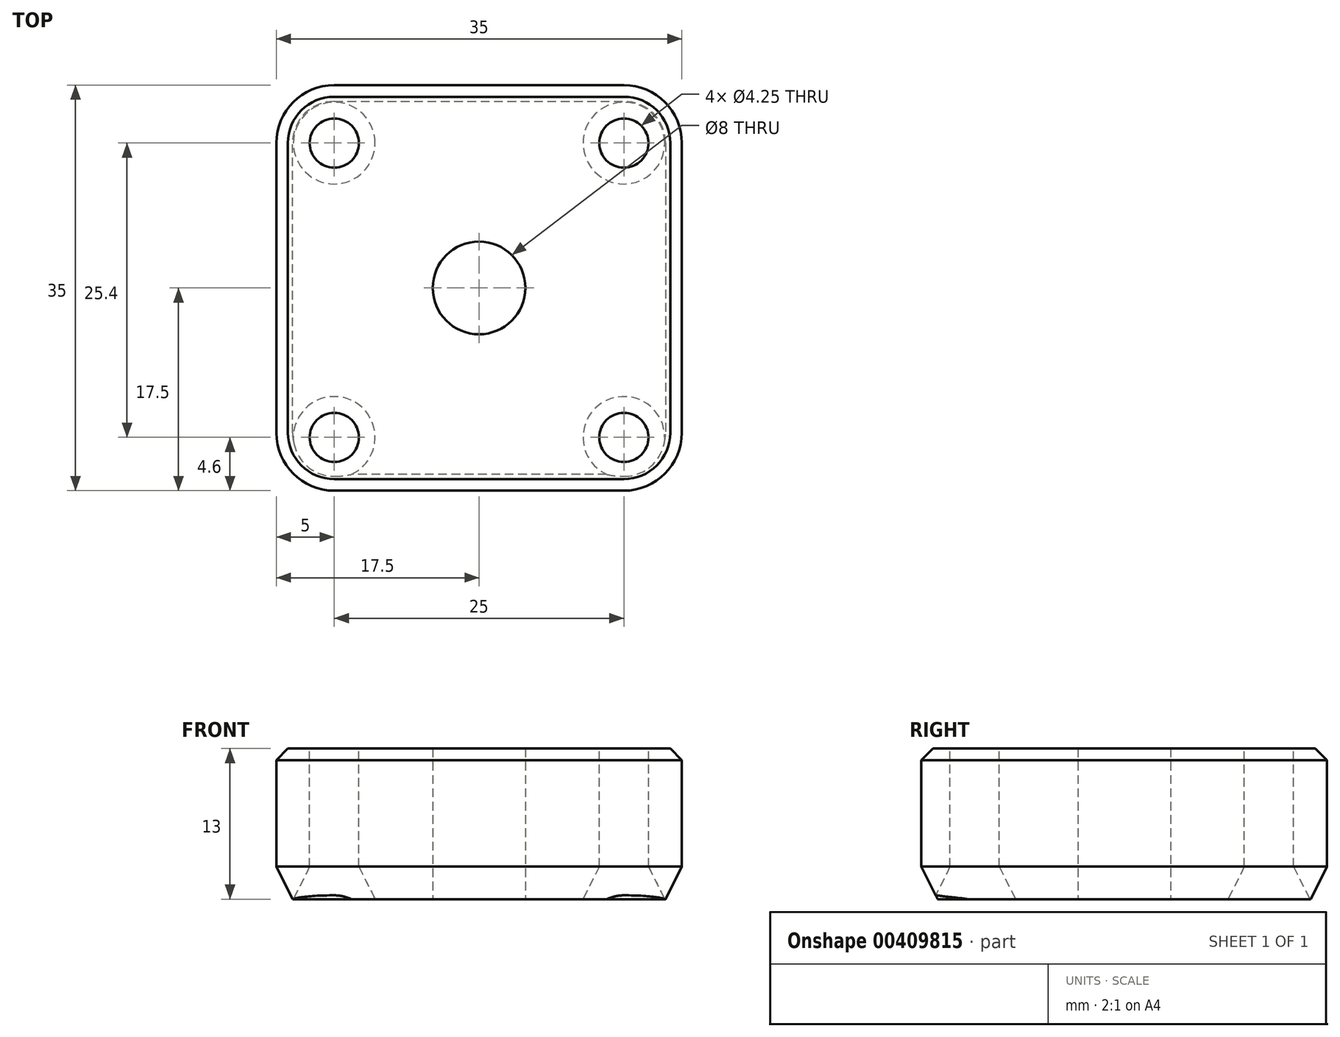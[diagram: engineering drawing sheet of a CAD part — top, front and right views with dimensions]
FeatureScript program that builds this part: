
annotation { "Feature Type Name" : "Feature", "Feature Type Description" : "" }
export const myFeature = defineFeature(function(context is Context, id is Id, definition is map)
    precondition{}
    {
        {
            var Q0;
            Q0=qCreatedBy(makeId("Top.planeOp"),FACE);
            var sketch = newSketch(context, id + "F0", { "sketchPlane" : qUnion([Q0])});
            skLineSegment(sketch, "E0.bottom", {"start": v(17.5, 17.5) * mm, "end": v(-17.5, 17.5) * mm});
            skLineSegment(sketch, "E0.top", {"start": v(17.5, -17.5) * mm, "end": v(-17.5, -17.5) * mm});
            skLineSegment(sketch, "E0.left", {"start": v(17.5, 17.5) * mm, "end": v(17.5, -17.5) * mm});
            skLineSegment(sketch, "E0.right", {"start": v(-17.5, 17.5) * mm, "end": v(-17.5, -17.5) * mm});
            skPoint(sketch, "E0.middle", {"position": v(0, 0) * mm});
            skSolve(sketch);
        }
        {
            var Q0;
            Q0=makeQuery(id+"F0.imprint","IMPRINT",FACE,{"disambiguationData":[TD([[makeQuery(id+"F0.imprint","IMPRINT",EDGE,{"derivedFrom":sQuery(id+"F0.wireOp",EDGE,"E0.bottom")}),1.0]])]});
            extrude(context, id + "F1", {"entities" : qUnion([Q0]), "endBound" : BoundingType.SYMMETRIC, "depth" : 13 * mm});
        }
        {
            var Q0;
            Q0=makeQuery(id+"F1.opExtrude","CAP_FACE",FACE,{"disambiguationData":[OSD([sQuery(id+"F0.wireOp",EDGE,"E0.bottom"),sQuery(id+"F0.wireOp",EDGE,"E0.top"),sQuery(id+"F0.wireOp",EDGE,"E0.left"),sQuery(id+"F0.wireOp",EDGE,"E0.right")])],"isStart":false});
            var sketch = newSketch(context, id + "F2", { "sketchPlane" : qUnion([Q0])});
            skCircle(sketch, "E1", {"center": v(-12.5, -12.9) * mm, "radius": 2.12 * mm});
            skCircle(sketch, "E2", {"center": v(-12.5, 12.5) * mm, "radius": 2.12 * mm});
            skCircle(sketch, "E3", {"center": v(12.5, 12.5) * mm, "radius": 2.12 * mm});
            skCircle(sketch, "E4", {"center": v(12.5, -12.9) * mm, "radius": 2.12 * mm});
            skSolve(sketch);
        }
        {
            var Q0;
            Q0=qSketchRegion(id+"F2",true);
            extrude(context, id + "F3", {"entities" : qUnion([Q0]), "operationType" : NewBodyOperationType.REMOVE, "endBound" : BoundingType.THROUGH_ALL, "oppositeDirection" : true, "depth" : 25 * mm});
        }
        {
            var Q0;
            Q0=makeQuery(id+"F1.opExtrude","SWEPT_EDGE",EDGE,{"disambiguationData":[OSD([sQuery(id+"F0.wireOp",EDGE,"E0.bottom"),sQuery(id+"F0.wireOp",EDGE,"E0.right")])]});
            var Q1;
            Q1=makeQuery(id+"F1.opExtrude","SWEPT_EDGE",EDGE,{"disambiguationData":[OSD([sQuery(id+"F0.wireOp",EDGE,"E0.bottom"),sQuery(id+"F0.wireOp",EDGE,"E0.left")])]});
            var Q2;
            Q2=makeQuery(id+"F1.opExtrude","SWEPT_EDGE",EDGE,{"disambiguationData":[OSD([sQuery(id+"F0.wireOp",EDGE,"E0.top"),sQuery(id+"F0.wireOp",EDGE,"E0.left")])]});
            var Q3;
            Q3=makeQuery(id+"F1.opExtrude","SWEPT_EDGE",EDGE,{"disambiguationData":[OSD([sQuery(id+"F0.wireOp",EDGE,"E0.top"),sQuery(id+"F0.wireOp",EDGE,"E0.right")])]});
            fillet(context, id + "F4", {"entities" : qUnion([Q0, Q1, Q2, Q3]), "radius" : 5 * mm, "tangentPropagation" : true, "allowEdgeOverflow" : false});
        }
        {
            var Q0;
            Q0=makeQuery(id+"F3.boolean.opBoolean","INTERSECT",EDGE,{"derivedFrom":[makeQuery(id+"F1.opExtrude","CAP_FACE",FACE,{"disambiguationData":[OSD([sQuery(id+"F0.wireOp",EDGE,"E0.bottom"),sQuery(id+"F0.wireOp",EDGE,"E0.top"),sQuery(id+"F0.wireOp",EDGE,"E0.left"),sQuery(id+"F0.wireOp",EDGE,"E0.right")])],"isStart":true}),makeQuery(id+"F3.opExtrude","SWEPT_FACE",FACE,{"disambiguationData":[OSD([sQuery(id+"F2.wireOp",EDGE,"E1")])]})]});
            var Q1;
            Q1=makeQuery(id+"F3.boolean.opBoolean","INTERSECT",EDGE,{"derivedFrom":[makeQuery(id+"F1.opExtrude","CAP_FACE",FACE,{"disambiguationData":[OSD([sQuery(id+"F0.wireOp",EDGE,"E0.bottom"),sQuery(id+"F0.wireOp",EDGE,"E0.top"),sQuery(id+"F0.wireOp",EDGE,"E0.left"),sQuery(id+"F0.wireOp",EDGE,"E0.right")])],"isStart":true}),makeQuery(id+"F3.opExtrude","SWEPT_FACE",FACE,{"disambiguationData":[OSD([sQuery(id+"F2.wireOp",EDGE,"E4")])]})]});
            var Q2;
            Q2=makeQuery(id+"F3.boolean.opBoolean","INTERSECT",EDGE,{"derivedFrom":[makeQuery(id+"F1.opExtrude","CAP_FACE",FACE,{"disambiguationData":[OSD([sQuery(id+"F0.wireOp",EDGE,"E0.bottom"),sQuery(id+"F0.wireOp",EDGE,"E0.top"),sQuery(id+"F0.wireOp",EDGE,"E0.left"),sQuery(id+"F0.wireOp",EDGE,"E0.right")])],"isStart":true}),makeQuery(id+"F3.opExtrude","SWEPT_FACE",FACE,{"disambiguationData":[OSD([sQuery(id+"F2.wireOp",EDGE,"E3")])]})]});
            var Q3;
            Q3=makeQuery(id+"F1.opExtrude","CAP_FACE",FACE,{"disambiguationData":[OSD([sQuery(id+"F0.wireOp",EDGE,"E0.bottom"),sQuery(id+"F0.wireOp",EDGE,"E0.top"),sQuery(id+"F0.wireOp",EDGE,"E0.left"),sQuery(id+"F0.wireOp",EDGE,"E0.right")])],"isStart":true});
            chamfer(context, id + "F5", {"entities" : qUnion([Q0, Q1, Q2, Q3]), "chamferType" : ChamferType.TWO_OFFSETS, "width1" : 1.4 * mm, "oppositeDirection" : false, "width2" : 2.8 * mm, "tangentPropagation" : true});
        }
        {
            var Q0;
            Q0=makeQuery(id+"F1.opExtrude","CAP_FACE",FACE,{"disambiguationData":[OSD([sQuery(id+"F0.wireOp",EDGE,"E0.bottom"),sQuery(id+"F0.wireOp",EDGE,"E0.top"),sQuery(id+"F0.wireOp",EDGE,"E0.left"),sQuery(id+"F0.wireOp",EDGE,"E0.right")])],"isStart":true});
            var sketch = newSketch(context, id + "F6", { "sketchPlane" : qUnion([Q0])});
            skCircle(sketch, "E5", {"center": v(0, 0) * mm, "radius": 4 * mm});
            skSolve(sketch);
        }
        {
            var Q0;
            Q0=qSketchRegion(id+"F6",true);
            extrude(context, id + "F7", {"entities" : qUnion([Q0]), "operationType" : NewBodyOperationType.REMOVE, "endBound" : BoundingType.THROUGH_ALL, "oppositeDirection" : true, "depth" : 25 * mm});
        }
        {
            var Q0;
            {var subQ0=sQuery(id+"F0.wireOp",EDGE,"E0.right");var subQ1=sQuery(id+"F0.wireOp",EDGE,"E0.top");Q0=makeQuery(id+"F4.opFillet","BLEND_EDGE",EDGE,{"blendedFrom":[makeQuery(id+"F1.opExtrude","SWEPT_EDGE",EDGE,{"disambiguationData":[OSD([subQ1,subQ0])]}),makeQuery(id+"F1.opExtrude","CAP_FACE",FACE,{"disambiguationData":[OSD([sQuery(id+"F0.wireOp",EDGE,"E0.bottom"),subQ1,sQuery(id+"F0.wireOp",EDGE,"E0.left"),subQ0])],"isStart":false})],"blendedInto":[makeQuery(id+"F1.opExtrude","CAP_FACE",FACE,{"disambiguationData":[OSD([sQuery(id+"F0.wireOp",EDGE,"E0.bottom"),subQ1,sQuery(id+"F0.wireOp",EDGE,"E0.left"),subQ0])],"isStart":false})]});}
            chamfer(context, id + "F8", {"entities" : qUnion([Q0]), "width" : 1 * mm, "tangentPropagation" : true});
        }
    });
